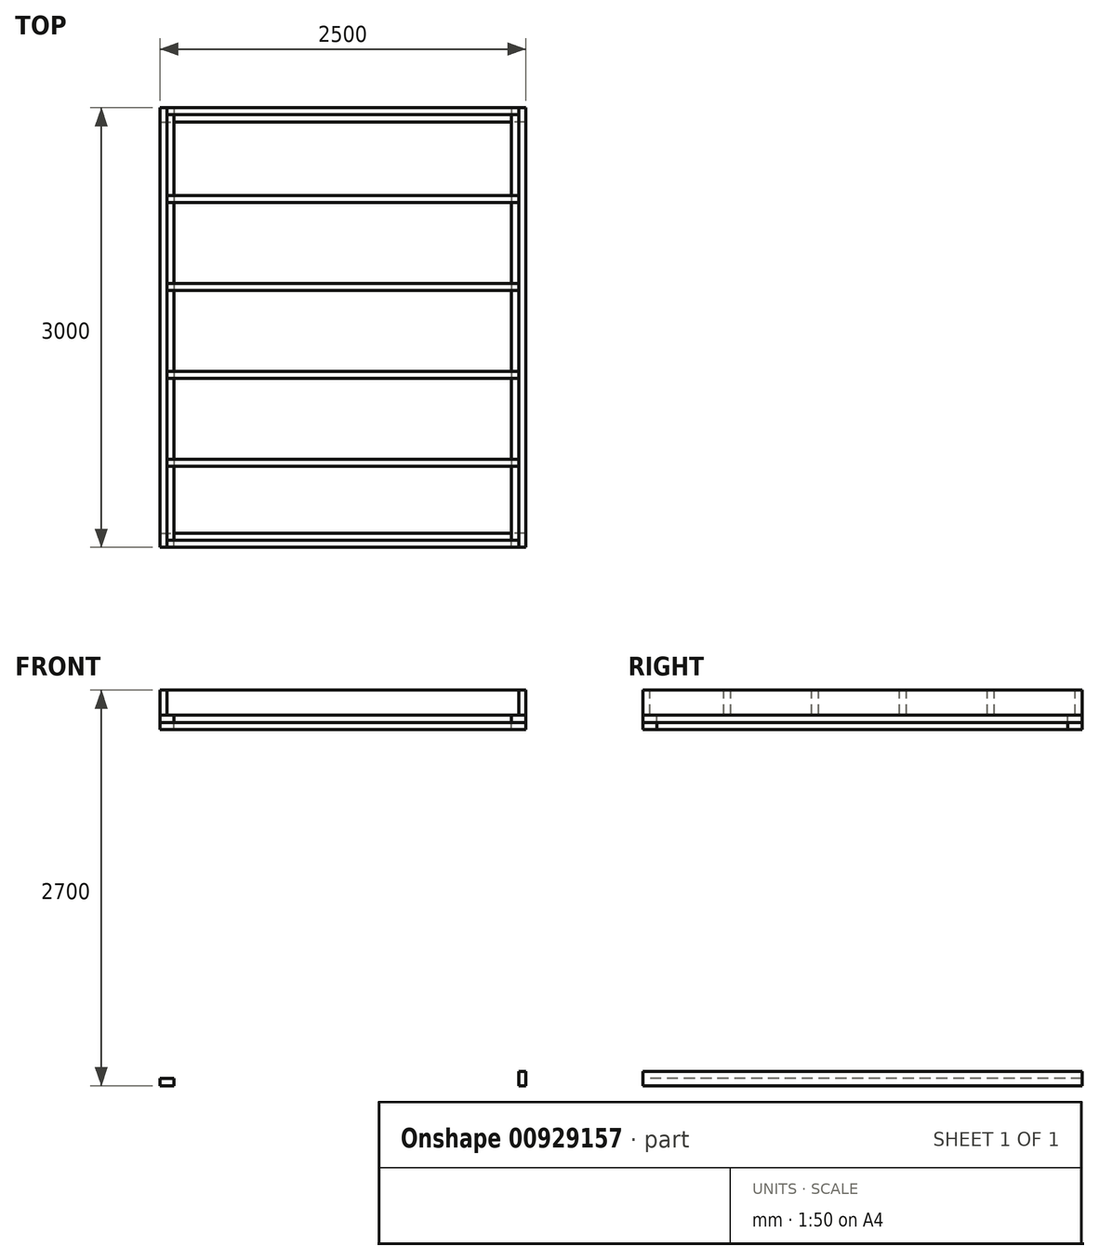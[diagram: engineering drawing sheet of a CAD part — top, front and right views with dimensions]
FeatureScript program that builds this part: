
annotation { "Feature Type Name" : "Feature", "Feature Type Description" : "" }
export const myFeature = defineFeature(function(context is Context, id is Id, definition is map)
    precondition{}
    {
        {
            assignVariable(context, id + "F0", {"name" : "poikkiparrun_korkeus", "anyValue" : 172});
        }
        {
            assignVariable(context, id + "F1", {"name" : "koolauspuun_paksuus", "anyValue" : 48});
        }
        {
            assignVariable(context, id + "F2", {"name" : "koolauspuun_korkeus", "anyValue" : 97});
        }
        {
            var Q0;
            Q0=qCreatedBy(makeId("Top.planeOp"),FACE);
            var sketch = newSketch(context, id + "F3", { "sketchPlane" : qUnion([Q0])});
            skLineSegment(sketch, "E0.bottom", {"start": v(0, 0) * mm, "end": v(-48, 0) * mm});
            skLineSegment(sketch, "E0.top", {"start": v(0, -3000) * mm, "end": v(-48, -3000) * mm});
            skLineSegment(sketch, "E0.left", {"start": v(0, 0) * mm, "end": v(0, -3000) * mm});
            skLineSegment(sketch, "E0.right", {"start": v(-48, 0) * mm, "end": v(-48, -3000) * mm});
            skLineSegment(sketch, "E1.bottom", {"start": v(-2452, 0) * mm, "end": v(-2500, 0) * mm});
            skLineSegment(sketch, "E1.top", {"start": v(-2452, -3000) * mm, "end": v(-2500, -3000) * mm});
            skLineSegment(sketch, "E1.left", {"start": v(-2452, 0) * mm, "end": v(-2452, -3000) * mm});
            skLineSegment(sketch, "E1.right", {"start": v(-2500, 0) * mm, "end": v(-2500, -3000) * mm});
            skSolve(sketch);
        }
        {
            var Q0;
            Q0=qSketchRegion(id+"F3",true);
            extrude(context, id + "F4", {"entities" : qUnion([Q0]), "oppositeDirection" : true, "depth" : (getVariable(context, 'poikkiparrun_korkeus')) * mm, "offsetDistance" : 25 * mm});
        }
        {
            var Q0;
            Q0=makeQuery(id+"F4.opExtrude","CAP_FACE",FACE,{"disambiguationData":[OSD([sQuery(id+"F3.wireOp",EDGE,"E0.bottom"),sQuery(id+"F3.wireOp",EDGE,"E0.top"),sQuery(id+"F3.wireOp",EDGE,"E0.left"),sQuery(id+"F3.wireOp",EDGE,"E0.right")])],"isStart":true});
            var sketch = newSketch(context, id + "F5", { "sketchPlane" : qUnion([Q0])});
            skLineSegment(sketch, "E2.bottom", {"start": v(-48, 0) * mm, "end": v(-2452, 0) * mm});
            skLineSegment(sketch, "E2.top", {"start": v(-48, -48) * mm, "end": v(-2452, -48) * mm});
            skLineSegment(sketch, "E2.left", {"start": v(-48, 0) * mm, "end": v(-48, -48) * mm});
            skLineSegment(sketch, "E2.right", {"start": v(-2452, 0) * mm, "end": v(-2452, -48) * mm});
            skLineSegment(sketch, "E3.0.1.0", {"start": v(-48, -648) * mm, "end": v(-2452, -648) * mm});
            skLineSegment(sketch, "E3.0.1.1", {"start": v(-48, -600) * mm, "end": v(-2452, -600) * mm});
            skLineSegment(sketch, "E3.0.1.2", {"start": v(-2452, -600) * mm, "end": v(-2452, -648) * mm});
            skLineSegment(sketch, "E3.0.1.3", {"start": v(-48, -600) * mm, "end": v(-48, -648) * mm});
            skLineSegment(sketch, "E3.direction1", {"start": v(-2452, -48) * mm, "end": v(-1872, -48) * mm, "construction": true});
            skLineSegment(sketch, "E3.direction2", {"start": v(-2452, -48) * mm, "end": v(-2452, -648) * mm, "construction": true});
            skLineSegment(sketch, "E4.0.0.2", {"start": v(-48, -1248) * mm, "end": v(-2452, -1248) * mm});
            skLineSegment(sketch, "E4.3.0.2", {"start": v(-48, -1200) * mm, "end": v(-2452, -1200) * mm});
            skLineSegment(sketch, "E4.6.0.2", {"start": v(-2452, -1200) * mm, "end": v(-2452, -1248) * mm});
            skLineSegment(sketch, "E4.9.0.2", {"start": v(-48, -1200) * mm, "end": v(-48, -1248) * mm});
            skLineSegment(sketch, "E4.0.0.3", {"start": v(-48, -1848) * mm, "end": v(-2452, -1848) * mm});
            skLineSegment(sketch, "E4.3.0.3", {"start": v(-48, -1800) * mm, "end": v(-2452, -1800) * mm});
            skLineSegment(sketch, "E4.6.0.3", {"start": v(-2452, -1800) * mm, "end": v(-2452, -1848) * mm});
            skLineSegment(sketch, "E4.9.0.3", {"start": v(-48, -1800) * mm, "end": v(-48, -1848) * mm});
            skLineSegment(sketch, "E4.0.0.4", {"start": v(-48, -2448) * mm, "end": v(-2452, -2448) * mm});
            skLineSegment(sketch, "E4.3.0.4", {"start": v(-48, -2400) * mm, "end": v(-2452, -2400) * mm});
            skLineSegment(sketch, "E4.6.0.4", {"start": v(-2452, -2400) * mm, "end": v(-2452, -2448) * mm});
            skLineSegment(sketch, "E4.9.0.4", {"start": v(-48, -2400) * mm, "end": v(-48, -2448) * mm});
            skLineSegment(sketch, "E5.bottom", {"start": v(-48, -3000) * mm, "end": v(-2452, -3000) * mm});
            skLineSegment(sketch, "E5.top", {"start": v(-48, -2952) * mm, "end": v(-2452, -2952) * mm});
            skLineSegment(sketch, "E5.left", {"start": v(-48, -3000) * mm, "end": v(-48, -2952) * mm});
            skLineSegment(sketch, "E5.right", {"start": v(-2452, -3000) * mm, "end": v(-2452, -2952) * mm});
            skSolve(sketch);
        }
        {
            var Q0;
            Q0=qSketchRegion(id+"F5",true);
            extrude(context, id + "F6", {"entities" : qUnion([Q0]), "oppositeDirection" : true, "depth" : (getVariable(context, 'poikkiparrun_korkeus')) * mm, "offsetDistance" : 25 * mm});
        }
        {
            var Q0;
            Q0=makeQuery(id+"F4.opExtrude","CAP_FACE",FACE,{"disambiguationData":[OSD([sQuery(id+"F3.wireOp",EDGE,"E0.bottom"),sQuery(id+"F3.wireOp",EDGE,"E0.top"),sQuery(id+"F3.wireOp",EDGE,"E0.left"),sQuery(id+"F3.wireOp",EDGE,"E0.right")])],"isStart":false});
            var sketch = newSketch(context, id + "F7", { "sketchPlane" : qUnion([Q0])});
            skLineSegment(sketch, "E6.bottom", {"start": v(0, 0) * mm, "end": v(-97, 0) * mm});
            skLineSegment(sketch, "E6.top", {"start": v(0, 3000) * mm, "end": v(-97, 3000) * mm});
            skLineSegment(sketch, "E6.left", {"start": v(0, 0) * mm, "end": v(0, 3000) * mm});
            skLineSegment(sketch, "E6.right", {"start": v(-97, 0) * mm, "end": v(-97, 3000) * mm});
            skLineSegment(sketch, "E7.bottom", {"start": v(-2500, 0) * mm, "end": v(-2403, 0) * mm});
            skLineSegment(sketch, "E7.top", {"start": v(-2500, 3000) * mm, "end": v(-2403, 3000) * mm});
            skLineSegment(sketch, "E7.left", {"start": v(-2500, 0) * mm, "end": v(-2500, 3000) * mm});
            skLineSegment(sketch, "E7.right", {"start": v(-2403, 0) * mm, "end": v(-2403, 3000) * mm});
            skSolve(sketch);
        }
        {
            var Q0;
            Q0=qSketchRegion(id+"F7",true);
            extrude(context, id + "F8", {"entities" : qUnion([Q0]), "depth" : (getVariable(context, 'koolauspuun_paksuus')) * mm, "offsetDistance" : 25 * mm});
        }
        {
            var Q0;
            Q0=makeQuery(id+"F6.opExtrude","CAP_FACE",FACE,{"disambiguationData":[OSD([sQuery(id+"F5.wireOp",EDGE,"E2.bottom"),sQuery(id+"F5.wireOp",EDGE,"E2.top"),sQuery(id+"F5.wireOp",EDGE,"E2.left"),sQuery(id+"F5.wireOp",EDGE,"E2.right")])],"isStart":false});
            var sketch = newSketch(context, id + "F9", { "sketchPlane" : qUnion([Q0])});
            skLineSegment(sketch, "E8.bottom", {"start": v(-2403, 0) * mm, "end": v(-97, 0) * mm});
            skLineSegment(sketch, "E8.top", {"start": v(-2403, 97) * mm, "end": v(-97, 97) * mm});
            skLineSegment(sketch, "E8.left", {"start": v(-2403, 0) * mm, "end": v(-2403, 97) * mm});
            skLineSegment(sketch, "E8.right", {"start": v(-97, 0) * mm, "end": v(-97, 97) * mm});
            skLineSegment(sketch, "E9.bottom", {"start": v(-97, 3000) * mm, "end": v(-2403, 3000) * mm});
            skLineSegment(sketch, "E9.top", {"start": v(-97, 2903) * mm, "end": v(-2403, 2903) * mm});
            skLineSegment(sketch, "E9.left", {"start": v(-97, 3000) * mm, "end": v(-97, 2903) * mm});
            skLineSegment(sketch, "E9.right", {"start": v(-2403, 3000) * mm, "end": v(-2403, 2903) * mm});
            skSolve(sketch);
        }
        {
            var Q0;
            Q0=qSketchRegion(id+"F9",true);
            extrude(context, id + "F10", {"entities" : qUnion([Q0]), "depth" : (getVariable(context, 'koolauspuun_paksuus')) * mm, "offsetDistance" : 25 * mm});
        }
        {
            var Q0;
            Q0=makeQuery(id+"F8.opExtrude","CAP_FACE",FACE,{"disambiguationData":[OSD([sQuery(id+"F7.wireOp",EDGE,"E7.bottom"),sQuery(id+"F7.wireOp",EDGE,"E7.top"),sQuery(id+"F7.wireOp",EDGE,"E7.left"),sQuery(id+"F7.wireOp",EDGE,"E7.right")])],"isStart":false});
            var sketch = newSketch(context, id + "F11", { "sketchPlane" : qUnion([Q0])});
            skLineSegment(sketch, "E10.bottom", {"start": v(-2500, 0) * mm, "end": v(0, 0) * mm});
            skLineSegment(sketch, "E10.top", {"start": v(-2500, 97) * mm, "end": v(0, 97) * mm});
            skLineSegment(sketch, "E10.left", {"start": v(-2500, 0) * mm, "end": v(-2500, 97) * mm});
            skLineSegment(sketch, "E10.right", {"start": v(0, 0) * mm, "end": v(0, 97) * mm});
            skLineSegment(sketch, "E11.bottom", {"start": v(0, 3000) * mm, "end": v(-2500, 3000) * mm});
            skLineSegment(sketch, "E11.top", {"start": v(0, 2903) * mm, "end": v(-2500, 2903) * mm});
            skLineSegment(sketch, "E11.left", {"start": v(0, 3000) * mm, "end": v(0, 2903) * mm});
            skLineSegment(sketch, "E11.right", {"start": v(-2500, 3000) * mm, "end": v(-2500, 2903) * mm});
            skSolve(sketch);
        }
        {
            var Q0;
            Q0=qSketchRegion(id+"F11",true);
            extrude(context, id + "F12", {"entities" : qUnion([Q0]), "depth" : (getVariable(context, 'koolauspuun_paksuus')) * mm, "offsetDistance" : 25 * mm});
        }
        {
            var Q0;
            Q0=makeQuery(id+"F8.opExtrude","CAP_FACE",FACE,{"disambiguationData":[OSD([sQuery(id+"F7.wireOp",EDGE,"E6.bottom"),sQuery(id+"F7.wireOp",EDGE,"E6.top"),sQuery(id+"F7.wireOp",EDGE,"E6.left"),sQuery(id+"F7.wireOp",EDGE,"E6.right")])],"isStart":false});
            var sketch = newSketch(context, id + "F13", { "sketchPlane" : qUnion([Q0])});
            skLineSegment(sketch, "E12.bottom", {"start": v(0, 2903) * mm, "end": v(-97, 2903) * mm});
            skLineSegment(sketch, "E12.top", {"start": v(0, 97) * mm, "end": v(-97, 97) * mm});
            skLineSegment(sketch, "E12.left", {"start": v(0, 2903) * mm, "end": v(0, 97) * mm});
            skLineSegment(sketch, "E12.right", {"start": v(-97, 2903) * mm, "end": v(-97, 97) * mm});
            skLineSegment(sketch, "E13.bottom", {"start": v(-2500, 2903) * mm, "end": v(-2403, 2903) * mm});
            skLineSegment(sketch, "E13.top", {"start": v(-2500, 97) * mm, "end": v(-2403, 97) * mm});
            skLineSegment(sketch, "E13.left", {"start": v(-2500, 2903) * mm, "end": v(-2500, 97) * mm});
            skLineSegment(sketch, "E13.right", {"start": v(-2403, 2903) * mm, "end": v(-2403, 97) * mm});
            skSolve(sketch);
        }
        {
            var Q0;
            Q0=qSketchRegion(id+"F13",true);
            extrude(context, id + "F14", {"entities" : qUnion([Q0]), "depth" : (getVariable(context, 'koolauspuun_paksuus')) * mm, "offsetDistance" : 25 * mm});
        }
        {
            var Q0;
            Q0=qCreatedBy(makeId("Right.planeOp"),FACE);
            var sketch = newSketch(context, id + "F15", { "sketchPlane" : qUnion([Q0])});
            skLineSegment(sketch, "E14.bottom", {"start": v(0, -2700) * mm, "end": v(-3000, -2700) * mm});
            skLineSegment(sketch, "E14.top", {"start": v(0, -2603) * mm, "end": v(-3000, -2603) * mm});
            skLineSegment(sketch, "E14.left", {"start": v(0, -2700) * mm, "end": v(0, -2603) * mm});
            skLineSegment(sketch, "E14.right", {"start": v(-3000, -2700) * mm, "end": v(-3000, -2603) * mm});
            skSolve(sketch);
        }
        {
            var Q0;
            Q0=qSketchRegion(id+"F15",true);
            extrude(context, id + "F16", {"entities" : qUnion([Q0]), "oppositeDirection" : true, "depth" : (getVariable(context, 'koolauspuun_paksuus')) * mm, "offsetDistance" : 25 * mm});
        }
        {
            var Q0;
            Q0=makeQuery(id+"F4.opExtrude","SWEPT_FACE",FACE,{"disambiguationData":[OSD([sQuery(id+"F3.wireOp",EDGE,"E1.right")])]});
            var sketch = newSketch(context, id + "F17", { "sketchPlane" : qUnion([Q0])});
            skLineSegment(sketch, "E15.bottom", {"start": v(0, -2700) * mm, "end": v(3000, -2700) * mm});
            skLineSegment(sketch, "E15.top", {"start": v(0, -2652) * mm, "end": v(3000, -2652) * mm});
            skLineSegment(sketch, "E15.left", {"start": v(0, -2700) * mm, "end": v(0, -2652) * mm});
            skLineSegment(sketch, "E15.right", {"start": v(3000, -2700) * mm, "end": v(3000, -2652) * mm});
            skSolve(sketch);
        }
        {
            var Q0;
            Q0=qSketchRegion(id+"F17",true);
            extrude(context, id + "F18", {"entities" : qUnion([Q0]), "oppositeDirection" : true, "depth" : (getVariable(context, 'koolauspuun_korkeus')) * mm, "offsetDistance" : 25 * mm});
        }
    });
